# Revit family: Шпалера «Лаватера» Арт 19538
name_source: partatom
category: Антураж
revit_build: Autodesk Revit 2018 (Build: 20180423_1000(x64)
units: mm (PartAtom-declared; Revit-internal decimal feet)

## family parameters
Всегда вертикально = Да
Источник визуального образа = Геометрия семейства
На основе рабочей плоскости = Нет
Общий = Нет
При загрузке вырезать с полостями = Нет
Точка расчета площади = Нет

## types (2) — shared parameters
URL = https://hobbyka.ru
Артикул товара = Арт. 19538
Высота = 1340 мм
Группа модели = Перголы и шпалеры
Длина = 1880 мм
Изготовитель = https://hobbyka.ru
Изображение типоразмера = Шпалера «Лаватера» Арт 19538.jpg
Материал изделия = Дерево
Ширина = 50 мм

## per-type parameters (varying)
| type | Без покраски | С покраской | Цвет каркаса |
| Шпалера «Лаватера». Версия 1880x1340 мм (без покраски) | Да | Нет | Дерево |
| Шпалера «Лаватера». Версия 1880x1340 мм (с покраской) | Нет | Да | Покраска |

note: column(s) folded — value = type name in every type: Описание
